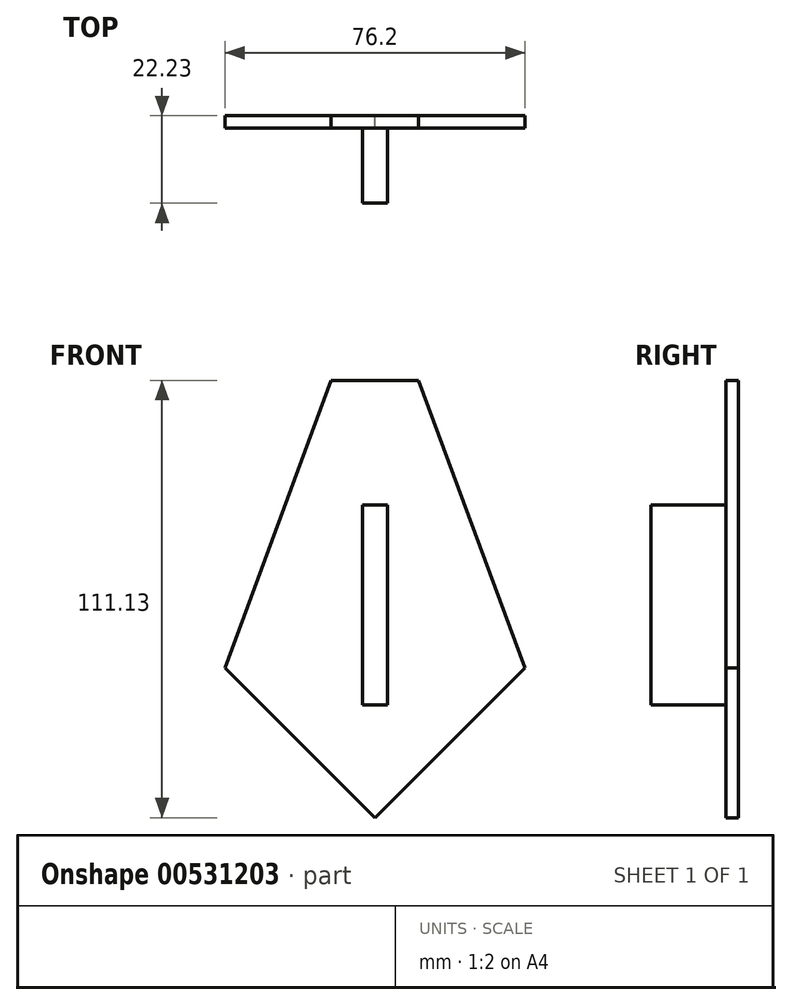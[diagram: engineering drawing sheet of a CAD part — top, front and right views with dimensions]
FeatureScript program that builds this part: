
annotation { "Feature Type Name" : "Feature", "Feature Type Description" : "" }
export const myFeature = defineFeature(function(context is Context, id is Id, definition is map)
    precondition{}
    {
        {
            var Q0;
            Q0=qCreatedBy(makeId("Front.planeOp"),FACE);
            var sketch = newSketch(context, id + "F0", { "sketchPlane" : qUnion([Q0])});
            skLineSegment(sketch, "E0", {"start": v(11.11, 73.03) * mm, "end": v(38.1, 0) * mm});
            skLineSegment(sketch, "E1", {"start": v(-11.11, 73.03) * mm, "end": v(-38.1, 0) * mm});
            skLineSegment(sketch, "E2", {"start": v(-38.1, 0) * mm, "end": v(0, -38.1) * mm});
            skLineSegment(sketch, "E3", {"start": v(0, -38.1) * mm, "end": v(38.1, 0) * mm});
            skLineSegment(sketch, "E4", {"start": v(-11.11, 73.03) * mm, "end": v(11.11, 73.03) * mm});
            skSolve(sketch);
        }
        {
            var Q0;
            Q0=makeQuery(id+"F0.imprint","IMPRINT",FACE,{"disambiguationData":[TD([[makeQuery(id+"F0.imprint","IMPRINT",EDGE,{"derivedFrom":sQuery(id+"F0.wireOp",EDGE,"E0")}),-1.0]])]});
            extrude(context, id + "F1", {"entities" : qUnion([Q0]), "depth" : 3.17 * mm, "offsetDistance" : 25.4 * mm});
        }
        {
            var Q0;
            Q0=makeQuery(id+"F1.opExtrude","CAP_FACE",FACE,{"disambiguationData":[OSD([sQuery(id+"F0.wireOp",EDGE,"E0"),sQuery(id+"F0.wireOp",EDGE,"E1"),sQuery(id+"F0.wireOp",EDGE,"E2"),sQuery(id+"F0.wireOp",EDGE,"E3"),sQuery(id+"F0.wireOp",EDGE,"E4")])],"isStart":false});
            var sketch = newSketch(context, id + "F2", { "sketchPlane" : qUnion([Q0])});
            skLineSegment(sketch, "E5.bottom", {"start": v(3.17, -9.43) * mm, "end": v(-3.18, -9.43) * mm});
            skLineSegment(sketch, "E5.top", {"start": v(3.17, 41.37) * mm, "end": v(-3.18, 41.37) * mm});
            skLineSegment(sketch, "E5.left", {"start": v(3.17, -9.43) * mm, "end": v(3.17, 41.37) * mm});
            skLineSegment(sketch, "E5.right", {"start": v(-3.18, -9.43) * mm, "end": v(-3.18, 41.37) * mm});
            skPoint(sketch, "E5.middle", {"position": v(0, 15.97) * mm});
            skSolve(sketch);
        }
        {
            var Q0;
            Q0 = qSketchRegion(id + "F2", true);
            extrude(context, id + "F3", {"entities" : qUnion([Q0]), "operationType" : NewBodyOperationType.ADD, "depth" : 19.05 * mm, "offsetDistance" : 25.4 * mm});
        }
    });
